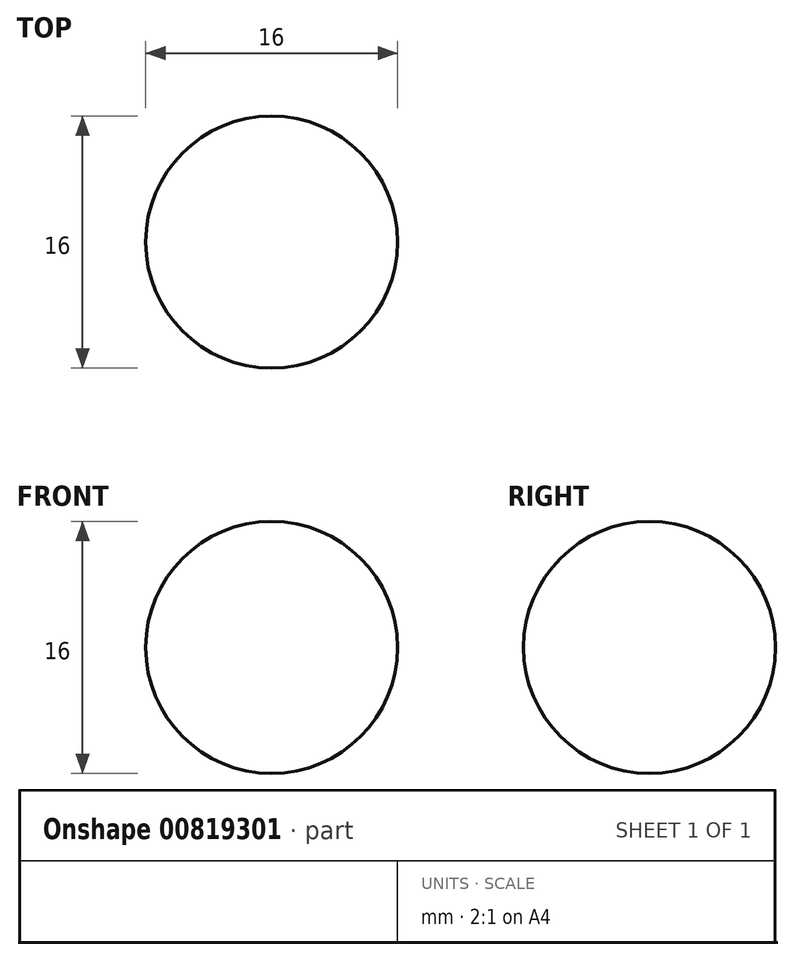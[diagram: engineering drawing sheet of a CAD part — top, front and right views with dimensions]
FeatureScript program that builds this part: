
annotation { "Feature Type Name" : "Feature", "Feature Type Description" : "" }
export const myFeature = defineFeature(function(context is Context, id is Id, definition is map)
    precondition{}
    {
        {
            var Q0;
            Q0=qCreatedBy(makeId("Front.planeOp"),FACE);
            var sketch = newSketch(context, id + "F0", { "sketchPlane" : qUnion([Q0])});
            skArc(sketch, "E0", {"start": v(0, -8) * mm, "mid": v(8, 0) * mm, "end": v(0, 8) * mm});
            skLineSegment(sketch, "E1", {"start": v(0, 8) * mm, "end": v(0, -8) * mm});
            skSolve(sketch);
        }
        {
            var Q0;
            Q0=makeQuery(id+"F0.imprint","IMPRINT",FACE,{"disambiguationData":[TD([[makeQuery(id+"F0.imprint","IMPRINT",EDGE,{"derivedFrom":sQuery(id+"F0.wireOp",EDGE,"E0")}),1.0]])]});
            var Q1;
            Q1=sQuery(id+"F0.wireOp",EDGE,"E1");
            revolve(context, id + "F1", {"surfaceOperationType" : NewSurfaceOperationType.NEW, "entities" : qUnion([Q0]), "axis" : qUnion([Q1]), "revolveType" : RevolveType.FULL});
        }
        {
            var Q0;
            Q0=makeQuery(id+"F1.opRevolve","SWEPT_BODY",BODY,{"disambiguationData":[OSD([sQuery(id+"F0.wireOp",EDGE,"E0"),sQuery(id+"F0.wireOp",EDGE,"E1")])]});
            transform(context, id + "F2", {"entities" : qUnion([Q0]), "transformType" : TransformType.TRANSLATION_3D, "dx" : 0 * mm, "dy" : 0 * mm, "dz" : 0 * mm, "makeCopy" : true});
        }
    });
